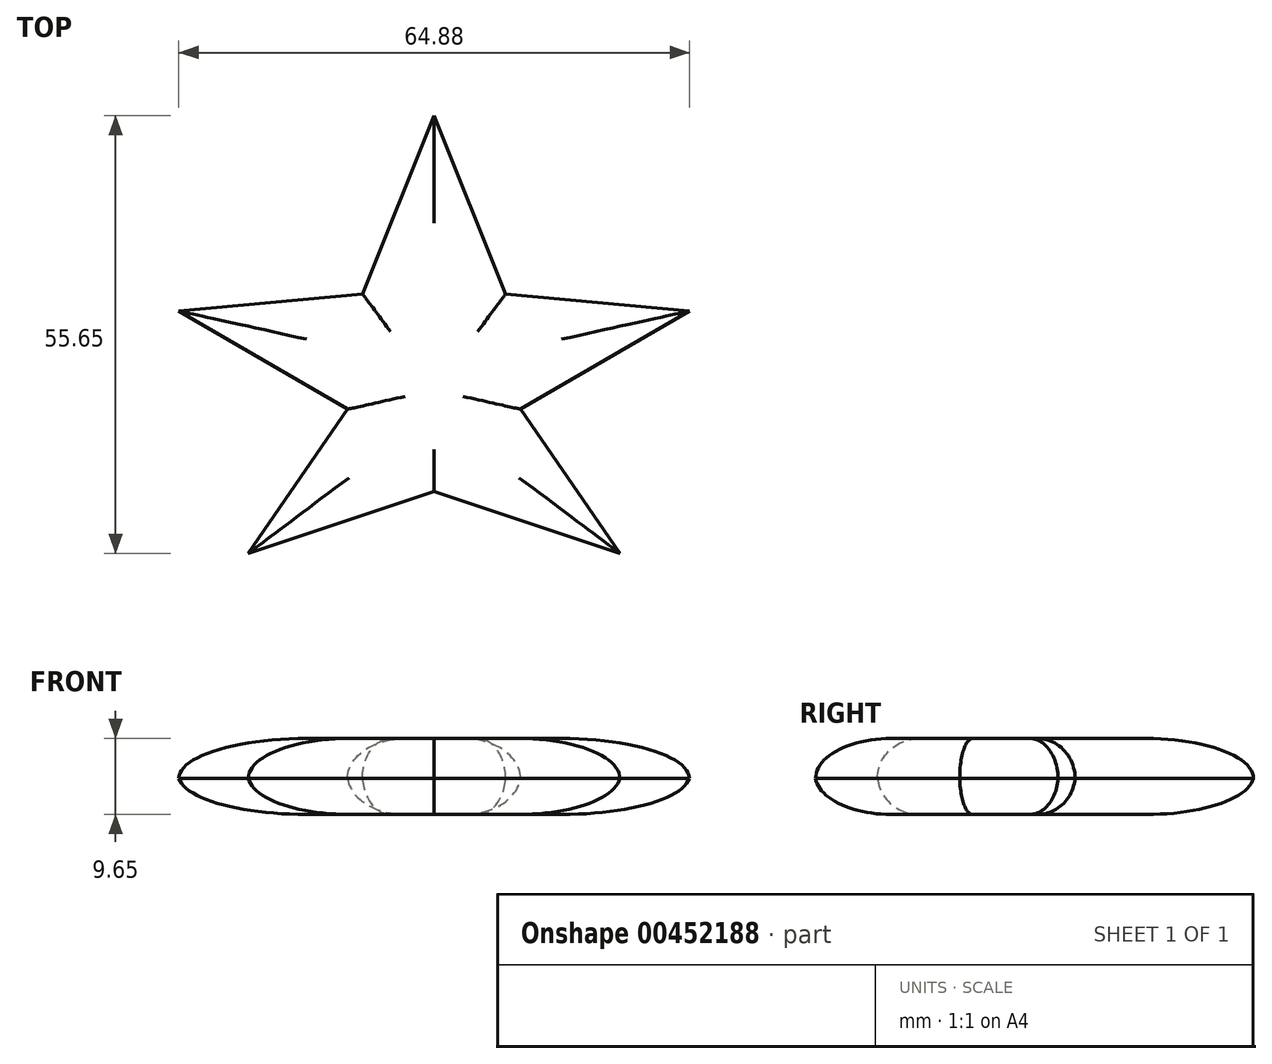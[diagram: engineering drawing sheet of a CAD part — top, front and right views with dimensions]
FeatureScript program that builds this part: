
annotation { "Feature Type Name" : "Feature", "Feature Type Description" : "" }
export const myFeature = defineFeature(function(context is Context, id is Id, definition is map)
    precondition{}
    {
        {
            var Q0;
            Q0=qCreatedBy(makeId("Top.planeOp"),FACE);
            var sketch = newSketch(context, id + "F0", { "sketchPlane" : qUnion([Q0])});
            skLineSegment(sketch, "E0", {"start": v(0, 40.65) * mm, "end": v(9.1, 17.98) * mm});
            skLineSegment(sketch, "E1", {"start": v(9.1, 17.98) * mm, "end": v(32.44, 15.81) * mm});
            skLineSegment(sketch, "E2", {"start": v(32.44, 15.81) * mm, "end": v(11, 3.33) * mm});
            skLineSegment(sketch, "E3", {"start": v(11, 3.33) * mm, "end": v(23.61, -15) * mm});
            skLineSegment(sketch, "E4", {"start": v(23.61, -15) * mm, "end": v(0, -7.13) * mm});
            skLineSegment(sketch, "E5.MirrorCS", {"start": v(-23.61, -15) * mm, "end": v(0, -7.13) * mm});
            skLineSegment(sketch, "E6.MirrorCS", {"start": v(-11, 3.33) * mm, "end": v(-23.61, -15) * mm});
            skLineSegment(sketch, "E7.MirrorCS", {"start": v(0, 40.65) * mm, "end": v(-9.1, 17.98) * mm});
            skLineSegment(sketch, "E8.MirrorCS", {"start": v(-9.1, 17.98) * mm, "end": v(-32.44, 15.81) * mm});
            skLineSegment(sketch, "E9.MirrorCS", {"start": v(-32.44, 15.81) * mm, "end": v(-11, 3.33) * mm});
            skSolve(sketch);
        }
        {
            var Q0;
            {var subQ0=sQuery(id+"F0.wireOp",EDGE,"E1");Q0=makeQuery(id+"F0.imprint","IMPRINT",FACE,{"disambiguationData":[TD([[makeQuery(id+"F0.imprint","IMPRINT",EDGE,{"derivedFrom":subQ0}),-1.0]])]});}
            extrude(context, id + "F1", {"entities" : qUnion([Q0]), "depth" : 9.65 * mm});
        }
        {
            var Q0;
            Q0=makeQuery(id+"F1.opExtrude","CAP_EDGE",EDGE,{"disambiguationData":[OSD([sQuery(id+"F0.wireOp",EDGE,"E2")])],"isStart":false});
            var Q1;
            Q1=makeQuery(id+"F1.opExtrude","CAP_EDGE",EDGE,{"disambiguationData":[OSD([sQuery(id+"F0.wireOp",EDGE,"E3")])],"isStart":false});
            var Q2;
            Q2=makeQuery(id+"F1.opExtrude","CAP_EDGE",EDGE,{"disambiguationData":[OSD([sQuery(id+"F0.wireOp",EDGE,"E4")])],"isStart":false});
            var Q3;
            Q3=makeQuery(id+"F1.opExtrude","CAP_EDGE",EDGE,{"disambiguationData":[OSD([sQuery(id+"F0.wireOp",EDGE,"E5.MirrorCS")])],"isStart":false});
            var Q4;
            Q4=makeQuery(id+"F1.opExtrude","CAP_EDGE",EDGE,{"disambiguationData":[OSD([sQuery(id+"F0.wireOp",EDGE,"E6.MirrorCS")])],"isStart":false});
            var Q5;
            Q5=makeQuery(id+"F1.opExtrude","CAP_EDGE",EDGE,{"disambiguationData":[OSD([sQuery(id+"F0.wireOp",EDGE,"E9.MirrorCS")])],"isStart":false});
            var Q6;
            Q6=makeQuery(id+"F1.opExtrude","CAP_EDGE",EDGE,{"disambiguationData":[OSD([sQuery(id+"F0.wireOp",EDGE,"E7.MirrorCS")])],"isStart":false});
            var Q7;
            Q7=makeQuery(id+"F1.opExtrude","CAP_EDGE",EDGE,{"disambiguationData":[OSD([sQuery(id+"F0.wireOp",EDGE,"E0")])],"isStart":false});
            var Q8;
            Q8=makeQuery(id+"F1.opExtrude","CAP_EDGE",EDGE,{"disambiguationData":[OSD([sQuery(id+"F0.wireOp",EDGE,"E1")])],"isStart":false});
            var Q9;
            Q9=makeQuery(id+"F1.opExtrude","CAP_EDGE",EDGE,{"disambiguationData":[OSD([sQuery(id+"F0.wireOp",EDGE,"E8.MirrorCS")])],"isStart":false});
            fillet(context, id + "F2", {"entities" : qUnion([Q0, Q1, Q2, Q3, Q4, Q5, Q6, Q7, Q8, Q9]), "radius" : 5.08 * mm, "tangentPropagation" : true, "allowEdgeOverflow" : false});
        }
        {
            var Q0;
            Q0=makeQuery(id+"F1.opExtrude","CAP_EDGE",EDGE,{"disambiguationData":[OSD([sQuery(id+"F0.wireOp",EDGE,"E1")])],"isStart":true});
            var Q1;
            Q1=makeQuery(id+"F1.opExtrude","CAP_EDGE",EDGE,{"disambiguationData":[OSD([sQuery(id+"F0.wireOp",EDGE,"E0")])],"isStart":true});
            var Q2;
            Q2=makeQuery(id+"F1.opExtrude","CAP_EDGE",EDGE,{"disambiguationData":[OSD([sQuery(id+"F0.wireOp",EDGE,"E7.MirrorCS")])],"isStart":true});
            var Q3;
            Q3=makeQuery(id+"F1.opExtrude","CAP_EDGE",EDGE,{"disambiguationData":[OSD([sQuery(id+"F0.wireOp",EDGE,"E8.MirrorCS")])],"isStart":true});
            var Q4;
            Q4=makeQuery(id+"F1.opExtrude","CAP_EDGE",EDGE,{"disambiguationData":[OSD([sQuery(id+"F0.wireOp",EDGE,"E9.MirrorCS")])],"isStart":true});
            var Q5;
            Q5=makeQuery(id+"F1.opExtrude","CAP_FACE",FACE,{"disambiguationData":[OSD([sQuery(id+"F0.wireOp",EDGE,"E0"),sQuery(id+"F0.wireOp",EDGE,"E1"),sQuery(id+"F0.wireOp",EDGE,"E2"),sQuery(id+"F0.wireOp",EDGE,"E3"),sQuery(id+"F0.wireOp",EDGE,"E4"),sQuery(id+"F0.wireOp",EDGE,"E5.MirrorCS"),sQuery(id+"F0.wireOp",EDGE,"E6.MirrorCS"),sQuery(id+"F0.wireOp",EDGE,"E7.MirrorCS"),sQuery(id+"F0.wireOp",EDGE,"E8.MirrorCS"),sQuery(id+"F0.wireOp",EDGE,"E9.MirrorCS")])],"isStart":true});
            var Q6;
            Q6=makeQuery(id+"F1.opExtrude","CAP_EDGE",EDGE,{"disambiguationData":[OSD([sQuery(id+"F0.wireOp",EDGE,"E6.MirrorCS")])],"isStart":true});
            var Q7;
            Q7=makeQuery(id+"F1.opExtrude","CAP_EDGE",EDGE,{"disambiguationData":[OSD([sQuery(id+"F0.wireOp",EDGE,"E5.MirrorCS")])],"isStart":true});
            fillet(context, id + "F3", {"entities" : qUnion([Q0, Q1, Q2, Q3, Q4, Q5, Q6, Q7]), "radius" : 5.08 * mm, "tangentPropagation" : true, "allowEdgeOverflow" : false});
        }
    });
